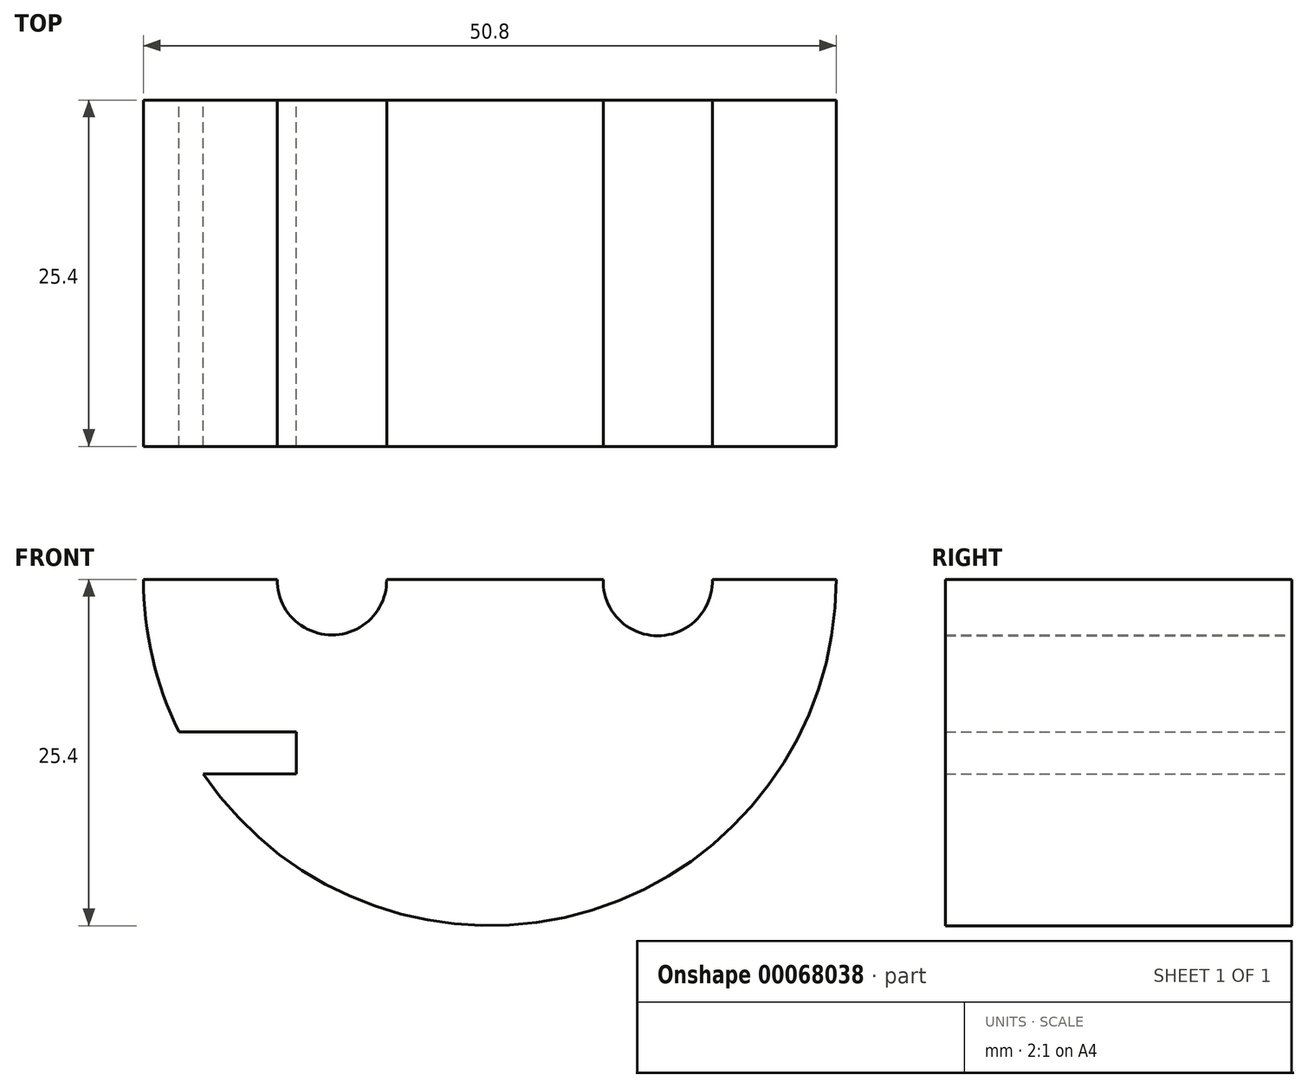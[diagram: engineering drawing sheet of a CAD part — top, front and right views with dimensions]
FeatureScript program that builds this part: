
annotation { "Feature Type Name" : "Feature", "Feature Type Description" : "" }
export const myFeature = defineFeature(function(context is Context, id is Id, definition is map)
    precondition{}
    {
        {
            var Q0;
            Q0=qCreatedBy(makeId("Front.planeOp"),FACE);
            var sketch = newSketch(context, id + "F0", { "sketchPlane" : qUnion([Q0])});
            skLineSegment(sketch, "E0", {"start": v(-39.22, 28.6) * mm, "end": v(-29.4, 28.6) * mm});
            skArc(sketch, "E1", {"start": v(-39.22, 28.6) * mm, "mid": v(-13.82, 3.2) * mm, "end": v(11.58, 28.6) * mm});
            skArc(sketch, "E2", {"start": v(-29.4, 28.6) * mm, "mid": v(-25.4, 24.52) * mm, "end": v(-21.4, 28.6) * mm});
            skArc(sketch, "E3", {"start": v(-5.52, 28.6) * mm, "mid": v(-1.51, 24.46) * mm, "end": v(2.5, 28.6) * mm});
            skLineSegment(sketch, "E4.trimOffspring", {"start": v(-21.4, 28.6) * mm, "end": v(-5.52, 28.6) * mm});
            skLineSegment(sketch, "E5.trimOffspring", {"start": v(2.5, 28.6) * mm, "end": v(11.58, 28.6) * mm});
            skLineSegment(sketch, "E6.bottom", {"start": v(-36.63, 17.41) * mm, "end": v(-28.02, 17.41) * mm});
            skLineSegment(sketch, "E6.top", {"start": v(-34.83, 14.32) * mm, "end": v(-28.02, 14.32) * mm});
            skLineSegment(sketch, "E6.right", {"start": v(-28.02, 17.41) * mm, "end": v(-28.02, 14.32) * mm});
            skSolve(sketch);
        }
        {
            var Q0;
            {var subQ3=sQuery(id+"F0.wireOp",EDGE,"E0");Q0=makeQuery(id+"F0.imprint","IMPRINT",FACE,{"disambiguationData":[TD([[makeQuery(id+"F0.imprint","IMPRINT",EDGE,{"derivedFrom":subQ3}),-1.0]])]});}
            extrude(context, id + "F1", {"entities" : qUnion([Q0]), "depth" : 25.4 * mm});
        }
    });
